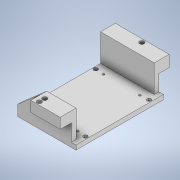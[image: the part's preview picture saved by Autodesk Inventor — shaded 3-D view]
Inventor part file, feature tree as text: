
AUTODESK INVENTOR PART (.ipt)
format: ipt  version: 2020 (Build 240168000, 168)  size: 229,888 bytes
history: native  units: mm
features: other x4, mirror x1
ambient origin geometry x8: Origin, YZ Plane, XZ Plane, XY Plane, X Axis, Y Axis, Z Axis, Center Point
bodies: Body1 (feature_tree)
feature tree (5):
  other  "tray4_R.ipt"
  mirror  "미러1"
  other  "솔리드1::tray4_R.ipt"
  other  "피쳐 태그1"
  other  "솔리드1"
